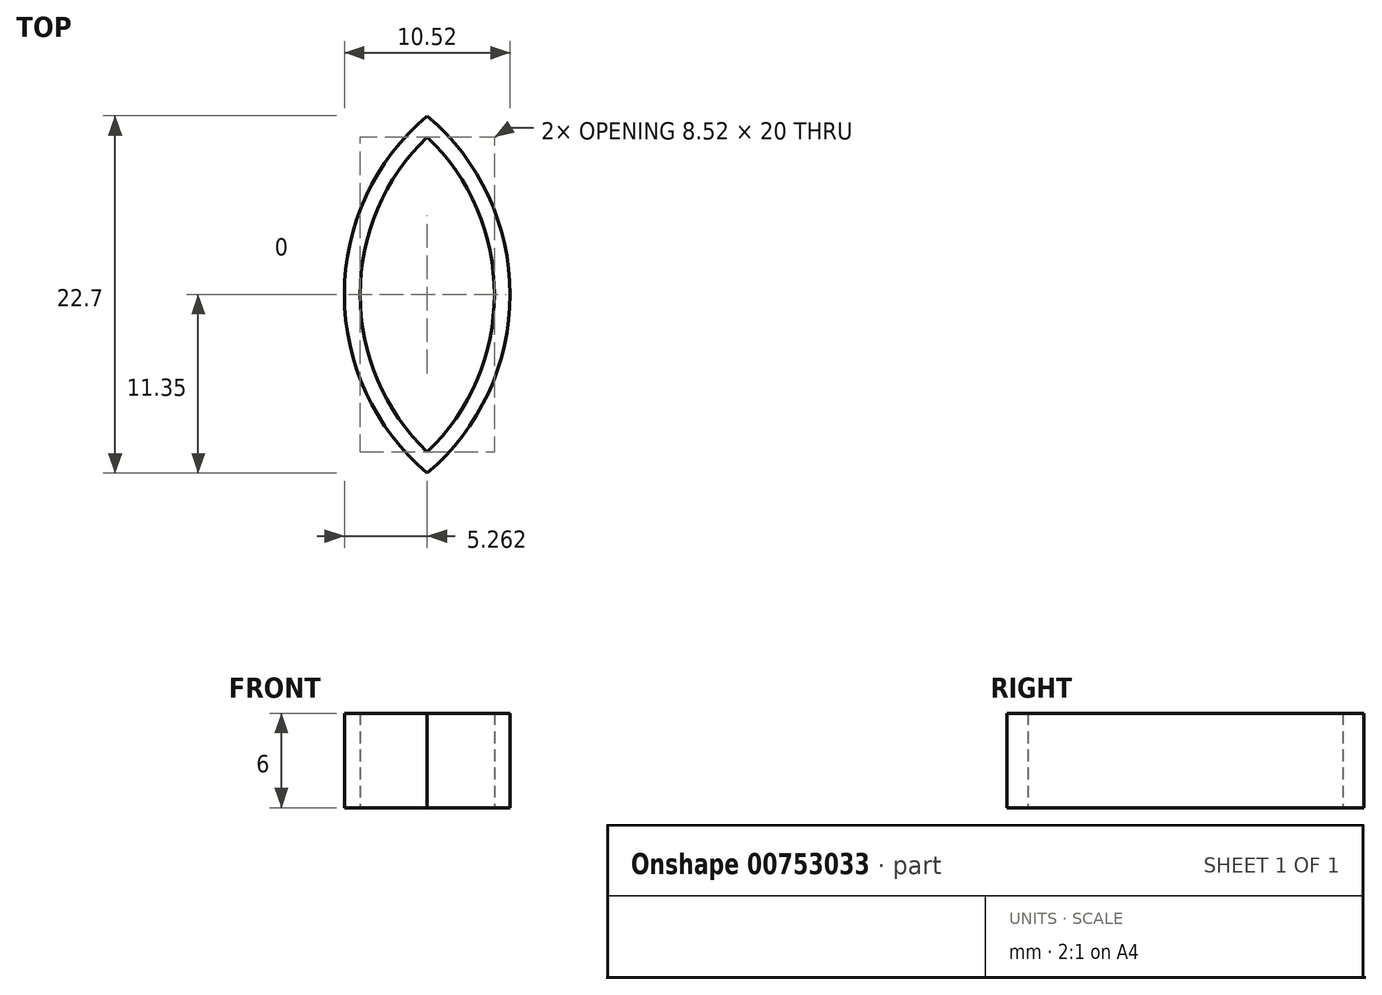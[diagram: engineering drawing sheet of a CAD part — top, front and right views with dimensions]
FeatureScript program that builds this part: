
annotation { "Feature Type Name" : "Feature", "Feature Type Description" : "" }
export const myFeature = defineFeature(function(context is Context, id is Id, definition is map)
    precondition{}
    {
        {
            var Q0;
            Q0=qCreatedBy(makeId("Top.planeOp"),FACE);
            var sketch = newSketch(context, id + "F0", { "sketchPlane" : qUnion([Q0])});
            skArc(sketch, "E0", {"start": v(1.55, -10) * mm, "mid": v(5.81, 0) * mm, "end": v(1.55, 10) * mm});
            skArc(sketch, "E1", {"start": v(1.55, 10) * mm, "mid": v(-2.71, 0) * mm, "end": v(1.55, -10) * mm});
            skLineSegment(sketch, "E2", {"start": v(1.55, 10) * mm, "end": v(1.55, -10) * mm, "construction": true});
            skArc(sketch, "E3.0", {"start": v(1.55, 11.35) * mm, "mid": v(-3.71, 0) * mm, "end": v(1.55, -11.35) * mm});
            skArc(sketch, "E3.1", {"start": v(1.55, -11.35) * mm, "mid": v(6.81, 0) * mm, "end": v(1.55, 11.35) * mm});
            skSolve(sketch);
        }
        {
            var Q0;
            Q0 = qSketchRegion(id + "F0", true);
            extrude(context, id + "F1", {"entities" : qUnion([Q0]), "depth" : 6 * mm, "offsetDistance" : 25 * mm});
        }
    });
